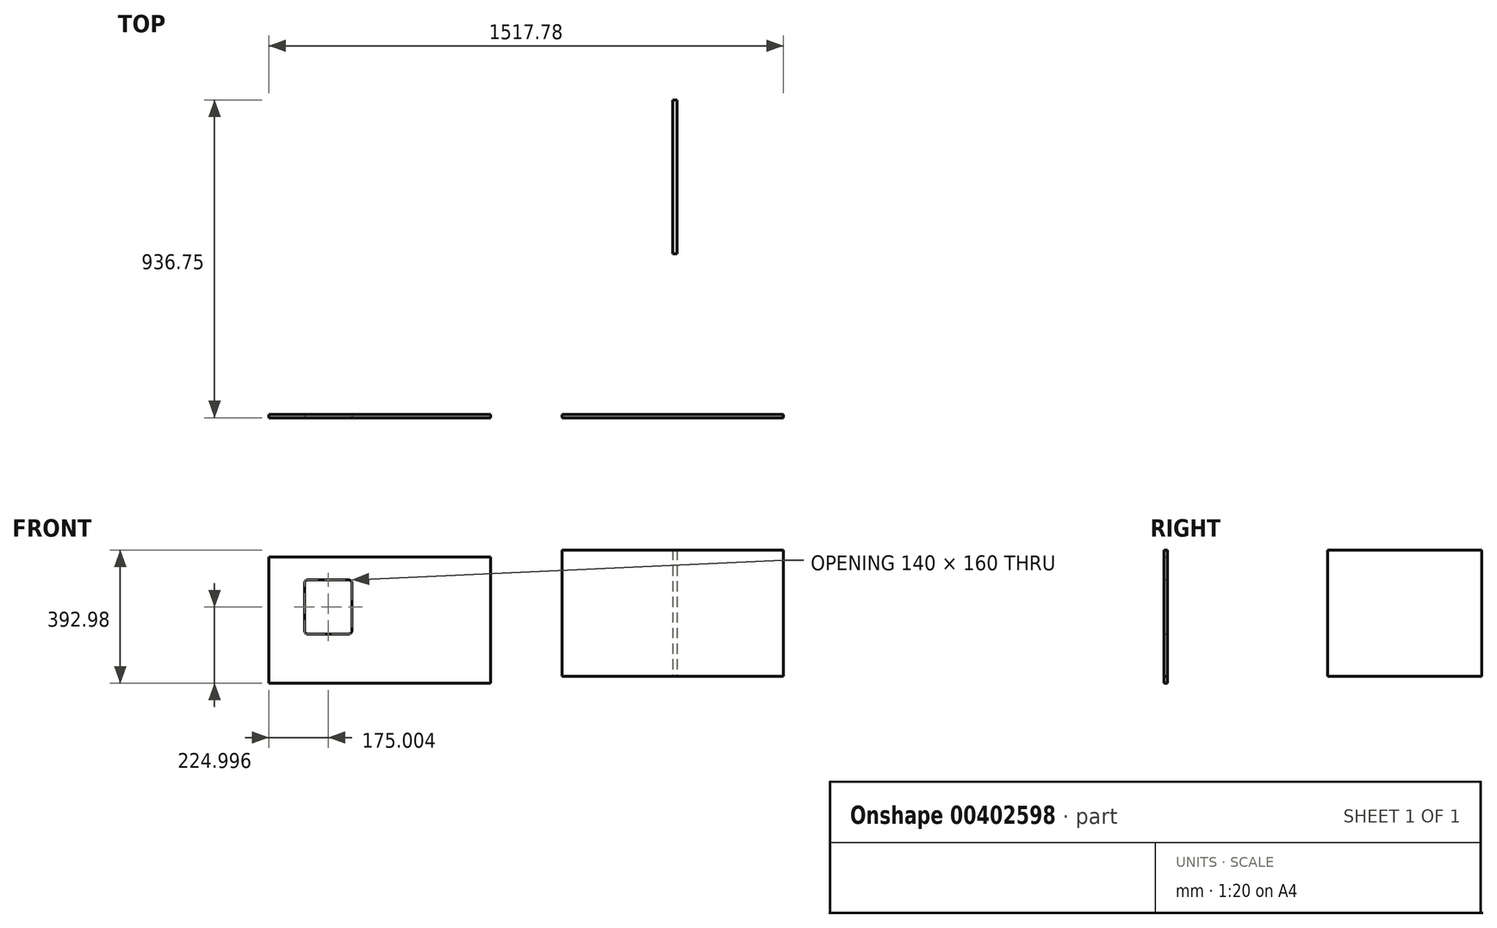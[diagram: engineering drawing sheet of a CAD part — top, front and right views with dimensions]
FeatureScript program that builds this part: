
annotation { "Feature Type Name" : "Feature", "Feature Type Description" : "" }
export const myFeature = defineFeature(function(context is Context, id is Id, definition is map)
    precondition{}
    {
        {
            var Q0;
            Q0=qCreatedBy(makeId("Front.planeOp"),FACE);
            var sketch = newSketch(context, id + "F0", { "sketchPlane" : qUnion([Q0])});
            skLineSegment(sketch, "E0.bottom", {"start": v(326.75, 186) * mm, "end": v(-326.75, 186) * mm});
            skLineSegment(sketch, "E0.top", {"start": v(326.75, -186) * mm, "end": v(-326.75, -186) * mm});
            skLineSegment(sketch, "E0.left", {"start": v(326.75, 186) * mm, "end": v(326.75, -186) * mm});
            skLineSegment(sketch, "E0.right", {"start": v(-326.75, 186) * mm, "end": v(-326.75, -186) * mm});
            skPoint(sketch, "E0.middle", {"position": v(0, 0) * mm});
            skLineSegment(sketch, "E1.bottom", {"start": v(-537.53, 165.02) * mm, "end": v(-1191.03, 165.02) * mm});
            skLineSegment(sketch, "E1.top", {"start": v(-537.53, -206.98) * mm, "end": v(-1191.03, -206.98) * mm});
            skLineSegment(sketch, "E1.left", {"start": v(-537.53, 165.02) * mm, "end": v(-537.53, -206.98) * mm});
            skLineSegment(sketch, "E1.right", {"start": v(-1191.03, 165.02) * mm, "end": v(-1191.03, -206.98) * mm});
            skPoint(sketch, "E1.middle", {"position": v(-864.28, -20.98) * mm});
            skSolve(sketch);
        }
        {
            var Q0;
            Q0=makeQuery(id+"F0.imprint","IMPRINT",FACE,{"disambiguationData":[TD([[makeQuery(id+"F0.imprint","IMPRINT",EDGE,{"derivedFrom":sQuery(id+"F0.wireOp",EDGE,"E0.bottom")}),1.0]])]});
            var Q1;
            Q1=makeQuery(id+"F0.imprint","IMPRINT",FACE,{"disambiguationData":[TD([[makeQuery(id+"F0.imprint","IMPRINT",EDGE,{"derivedFrom":sQuery(id+"F0.wireOp",EDGE,"E1.bottom")}),1.0]])]});
            extrude(context, id + "F1", {"entities" : qUnion([Q0, Q1]), "depth" : 10 * mm});
        }
        {
            var Q0;
            Q0=qCreatedBy(makeId("Right.planeOp"),FACE);
            var sketch = newSketch(context, id + "F2", { "sketchPlane" : qUnion([Q0])});
            skLineSegment(sketch, "E2", {"start": v(0, 0) * mm, "end": v(700, 0) * mm});
            skLineSegment(sketch, "E3.bottom", {"start": v(473.25, 186) * mm, "end": v(926.75, 186) * mm});
            skLineSegment(sketch, "E3.top", {"start": v(473.25, -186) * mm, "end": v(926.75, -186) * mm});
            skLineSegment(sketch, "E3.left", {"start": v(473.25, 186) * mm, "end": v(473.25, -186) * mm});
            skLineSegment(sketch, "E3.right", {"start": v(926.75, 186) * mm, "end": v(926.75, -186) * mm});
            skPoint(sketch, "E3.middle", {"position": v(700, 0) * mm});
            skSolve(sketch);
        }
        {
            var Q0;
            {var subQ0=sQuery(id+"F2.wireOp",EDGE,"E3.bottom");Q0=makeQuery(id+"F2.imprint","IMPRINT",FACE,{"disambiguationData":[TD([[makeQuery(id+"F2.imprint","IMPRINT",EDGE,{"derivedFrom":subQ0}),-1.0]])]});}
            extrude(context, id + "F3", {"entities" : qUnion([Q0]), "depth" : 12.5 * mm});
        }
        {
            var Q0;
            Q0=makeQuery(id+"F1.opExtrude","CAP_FACE",FACE,{"disambiguationData":[OSD([sQuery(id+"F0.wireOp",EDGE,"E1.bottom"),sQuery(id+"F0.wireOp",EDGE,"E1.top"),sQuery(id+"F0.wireOp",EDGE,"E1.left"),sQuery(id+"F0.wireOp",EDGE,"E1.right")])],"isStart":false});
            var sketch = newSketch(context, id + "F4", { "sketchPlane" : qUnion([Q0])});
            skLineSegment(sketch, "E4.bottom", {"start": v(-1196.03, -206.98) * mm, "end": v(-532.53, -206.98) * mm});
            skLineSegment(sketch, "E4.top", {"start": v(-1196.03, 168.02) * mm, "end": v(-532.53, 168.02) * mm});
            skLineSegment(sketch, "E4.left", {"start": v(-1196.03, -206.98) * mm, "end": v(-1196.03, 168.02) * mm});
            skLineSegment(sketch, "E4.right", {"start": v(-532.53, -206.98) * mm, "end": v(-532.53, 168.02) * mm});
            skLineSegment(sketch, "E5", {"start": v(-532.53, -206.98) * mm, "end": v(-682.53, -206.98) * mm});
            skLineSegment(sketch, "E6.bottom", {"start": v(-956.03, 98.02) * mm, "end": v(-1076.03, 98.02) * mm});
            skLineSegment(sketch, "E6.top", {"start": v(-956.03, -61.98) * mm, "end": v(-1076.03, -61.98) * mm});
            skLineSegment(sketch, "E6.left", {"start": v(-946.03, 88.02) * mm, "end": v(-946.03, -51.98) * mm});
            skLineSegment(sketch, "E6.right", {"start": v(-1086.03, 88.02) * mm, "end": v(-1086.03, -51.98) * mm});
            skPoint(sketch, "E6.middle", {"position": v(-1016.03, 18.02) * mm});
            skPoint(sketch, "E7.visualSharp", {"position": v(-1086.03, 98.02) * mm});
            skArc(sketch, "E7.filletArc", {"start": v(-1076.03, 98.02) * mm, "mid": v(-1083.1, 95.09) * mm, "end": v(-1086.03, 88.02) * mm});
            skPoint(sketch, "E8.visualSharp", {"position": v(-946.03, 98.02) * mm});
            skArc(sketch, "E8.filletArc", {"start": v(-946.03, 88.02) * mm, "mid": v(-948.96, 95.09) * mm, "end": v(-956.03, 98.02) * mm});
            skPoint(sketch, "E9.visualSharp", {"position": v(-1086.03, -61.98) * mm});
            skArc(sketch, "E9.filletArc", {"start": v(-1086.03, -51.98) * mm, "mid": v(-1083.1, -59.06) * mm, "end": v(-1076.03, -61.98) * mm});
            skPoint(sketch, "E10.visualSharp", {"position": v(-946.03, -61.98) * mm});
            skArc(sketch, "E10.filletArc", {"start": v(-956.03, -61.98) * mm, "mid": v(-948.96, -59.06) * mm, "end": v(-946.03, -51.98) * mm});
            skLineSegment(sketch, "E11.bottom", {"start": v(-682.53, -206.98) * mm, "end": v(-882.53, -206.98) * mm});
            skLineSegment(sketch, "E11.left", {"start": v(-682.53, -206.98) * mm, "end": v(-682.53, -6.98) * mm});
            skLineSegment(sketch, "E11.right", {"start": v(-882.53, -206.98) * mm, "end": v(-882.53, -6.98) * mm});
            skPoint(sketch, "E12.visualSharp", {"position": v(-882.53, 93.02) * mm});
            skArc(sketch, "E12.filletArc", {"start": v(-782.53, 93.02) * mm, "mid": v(-853.24, 63.73) * mm, "end": v(-882.53, -6.98) * mm});
            skPoint(sketch, "E13.visualSharp", {"position": v(-682.53, 93.02) * mm});
            skArc(sketch, "E13.filletArc", {"start": v(-682.53, -6.98) * mm, "mid": v(-711.82, 63.73) * mm, "end": v(-782.53, 93.02) * mm});
            skLineSegment(sketch, "E14", {"start": v(-1191.03, 165.02) * mm, "end": v(-537.53, 165.02) * mm});
            skLineSegment(sketch, "E15", {"start": v(-1196.03, -206.98) * mm, "end": v(-1191.03, -206.98) * mm});
            skSolve(sketch);
        }
        {
            var Q0;
            Q0=makeQuery(id+"F4.imprint","IMPRINT",FACE,{"disambiguationData":[TD([[makeQuery(id+"F4.imprint","IMPRINT",EDGE,{"derivedFrom":sQuery(id+"F4.wireOp",EDGE,"E6.bottom")}),1.0]])]});
            var Q1;
            Q1=makeQuery(id+"F4.imprint","IMPRINT",FACE,{"disambiguationData":[TD([[makeQuery(id+"F4.imprint","IMPRINT",EDGE,{"derivedFrom":sQuery(id+"F4.wireOp",EDGE,"E11.bottom")}),-1.0]])]});
            extrude(context, id + "F5", {"entities" : qUnion([Q0, Q1]), "operationType" : NewBodyOperationType.REMOVE, "oppositeDirection" : true, "depth" : 10 * mm});
        }
    });
